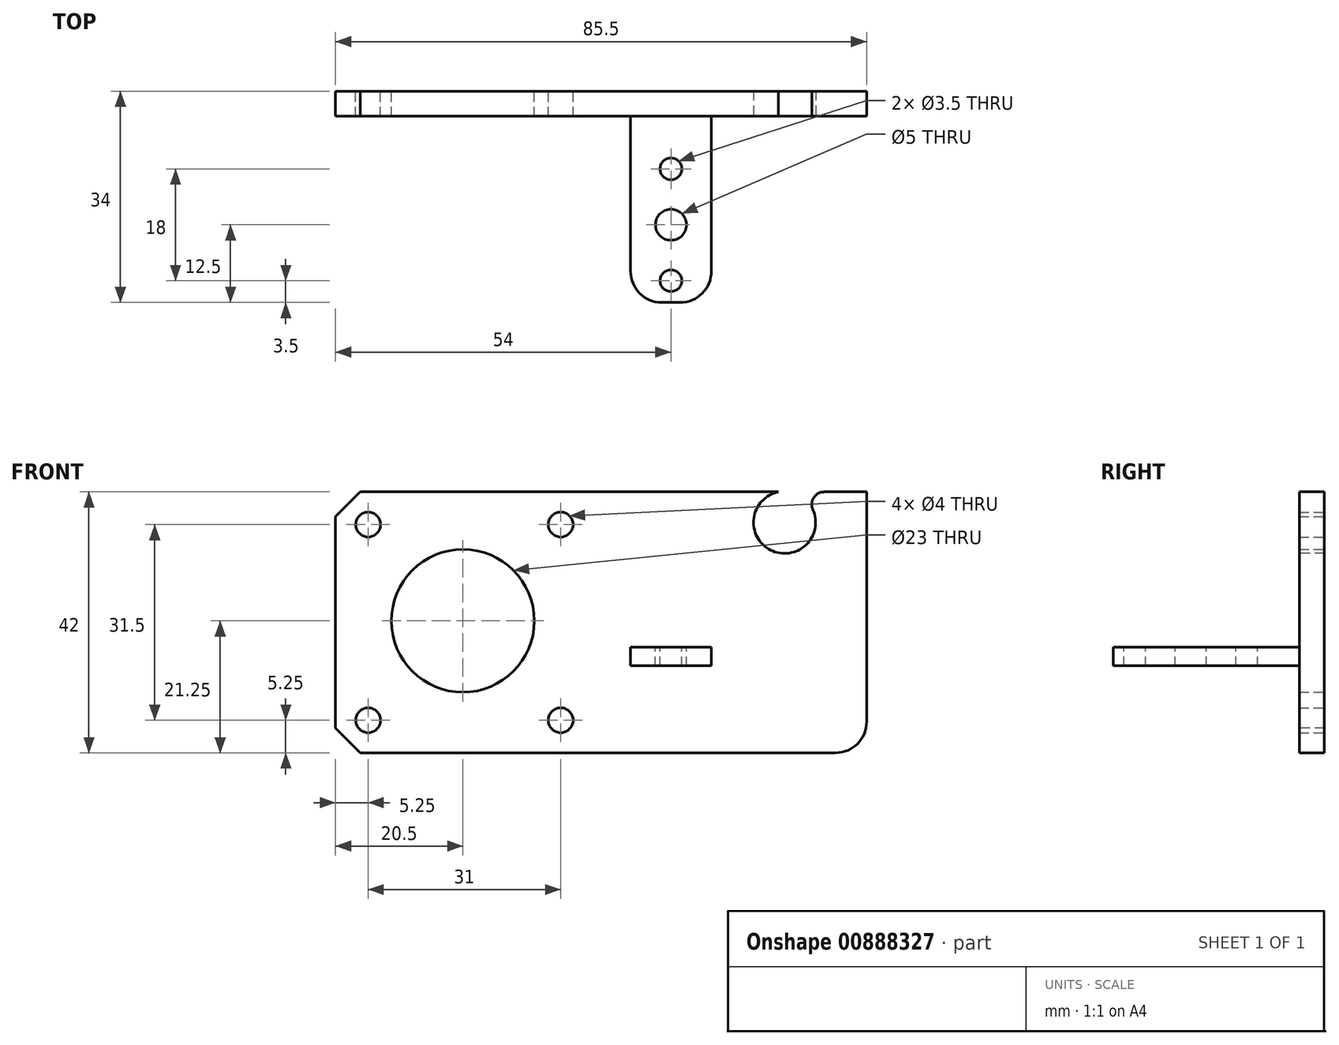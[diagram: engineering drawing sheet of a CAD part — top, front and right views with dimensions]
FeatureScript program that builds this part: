
annotation { "Feature Type Name" : "Feature", "Feature Type Description" : "" }
export const myFeature = defineFeature(function(context is Context, id is Id, definition is map)
    precondition{}
    {
        {
            var Q0;
            Q0=qCreatedBy(makeId("Front.planeOp"),FACE);
            var sketch = newSketch(context, id + "F0", { "sketchPlane" : qUnion([Q0])});
            skLineSegment(sketch, "E0.bottom", {"start": v(43, -21.25) * mm, "end": v(-20.5, -21.25) * mm});
            skLineSegment(sketch, "E0.top", {"start": v(43, 20.75) * mm, "end": v(-20.5, 20.75) * mm});
            skLineSegment(sketch, "E0.left", {"start": v(43, -21.25) * mm, "end": v(43, 20.75) * mm});
            skLineSegment(sketch, "E0.right", {"start": v(-20.5, -21.25) * mm, "end": v(-20.5, 20.75) * mm});
            skPoint(sketch, "E0.middle", {"position": v(0, 0) * mm});
            skCircle(sketch, "E1", {"center": v(0, 0) * mm, "radius": 11.5 * mm});
            skCircle(sketch, "E2", {"center": v(-15.25, 15.5) * mm, "radius": 2 * mm});
            skCircle(sketch, "E3", {"center": v(15.75, 15.5) * mm, "radius": 2 * mm});
            skCircle(sketch, "E4", {"center": v(-15.25, -16) * mm, "radius": 2 * mm});
            skCircle(sketch, "E5", {"center": v(15.75, -16) * mm, "radius": 2 * mm});
            skSolve(sketch);
        }
        {
            var Q0;
            Q0=makeQuery(id+"F0.imprint","IMPRINT",FACE,{"disambiguationData":[TD([[makeQuery(id+"F0.imprint","IMPRINT",EDGE,{"derivedFrom":sQuery(id+"F0.wireOp",EDGE,"E0.bottom")}),-1.0]])]});
            extrude(context, id + "F1", {"entities" : qUnion([Q0]), "depth" : 4 * mm, "offsetDistance" : 25 * mm});
        }
        {
            var Q0;
            Q0=makeQuery(id+"F1.opExtrude","SWEPT_EDGE",EDGE,{"disambiguationData":[OSD([sQuery(id+"F0.wireOp",EDGE,"E0.bottom"),sQuery(id+"F0.wireOp",EDGE,"E0.right")])]});
            var Q1;
            Q1=makeQuery(id+"F1.opExtrude","SWEPT_EDGE",EDGE,{"disambiguationData":[OSD([sQuery(id+"F0.wireOp",EDGE,"E0.top"),sQuery(id+"F0.wireOp",EDGE,"E0.right")])]});
            chamfer(context, id + "F2", {"entities" : qUnion([Q0, Q1]), "width" : 4 * mm, "tangentPropagation" : true});
        }
        {
            var Q0;
            Q0=makeQuery(id+"F1.opExtrude","CAP_FACE",FACE,{"disambiguationData":[OSD([sQuery(id+"F0.wireOp",EDGE,"E0.bottom"),sQuery(id+"F0.wireOp",EDGE,"E0.top"),sQuery(id+"F0.wireOp",EDGE,"E0.left"),sQuery(id+"F0.wireOp",EDGE,"E0.right"),sQuery(id+"F0.wireOp",EDGE,"E1"),sQuery(id+"F0.wireOp",EDGE,"E2"),sQuery(id+"F0.wireOp",EDGE,"E3"),sQuery(id+"F0.wireOp",EDGE,"E4"),sQuery(id+"F0.wireOp",EDGE,"E5")])],"isStart":false});
            var sketch = newSketch(context, id + "F3", { "sketchPlane" : qUnion([Q0])});
            skLineSegment(sketch, "E6.bottom", {"start": v(27, -4.25) * mm, "end": v(40, -4.25) * mm});
            skLineSegment(sketch, "E6.top", {"start": v(27, -7.25) * mm, "end": v(40, -7.25) * mm});
            skLineSegment(sketch, "E6.left", {"start": v(27, -4.25) * mm, "end": v(27, -7.25) * mm});
            skLineSegment(sketch, "E6.right", {"start": v(40, -4.25) * mm, "end": v(40, -7.25) * mm});
            skSolve(sketch);
        }
        {
            var Q0;
            Q0=qSketchRegion(id+"F3",true);
            extrude(context, id + "F4", {"entities" : qUnion([Q0]), "operationType" : NewBodyOperationType.ADD, "depth" : 30 * mm, "offsetDistance" : 25 * mm});
        }
        {
            var Q0;
            Q0=makeQuery(id+"F4.opExtrude","CAP_EDGE",EDGE,{"disambiguationData":[OSD([sQuery(id+"F3.wireOp",EDGE,"E6.right")])],"isStart":false});
            var Q1;
            Q1=makeQuery(id+"F4.opExtrude","CAP_EDGE",EDGE,{"disambiguationData":[OSD([sQuery(id+"F3.wireOp",EDGE,"E6.left")])],"isStart":false});
            fillet(context, id + "F5", {"entities" : qUnion([Q0, Q1]), "radius" : 5 * mm, "tangentPropagation" : true, "allowEdgeOverflow" : false});
        }
        {
            var Q0;
            Q0=makeQuery(id+"F4.opExtrude","SWEPT_FACE",FACE,{"disambiguationData":[OSD([sQuery(id+"F3.wireOp",EDGE,"E6.bottom")])]});
            var sketch = newSketch(context, id + "F6", { "sketchPlane" : qUnion([Q0])});
            skCircle(sketch, "E7", {"center": v(33.5, -21.5) * mm, "radius": 2.5 * mm});
            skCircle(sketch, "E8", {"center": v(33.5, -30.5) * mm, "radius": 1.75 * mm});
            skCircle(sketch, "E9", {"center": v(33.5, -12.5) * mm, "radius": 1.75 * mm});
            skLineSegment(sketch, "E10", {"start": v(33.5, -4) * mm, "end": v(33.5, -34) * mm, "construction": true});
            skSolve(sketch);
        }
        {
            var Q0;
            Q0=qSketchRegion(id+"F6",true);
            extrude(context, id + "F7", {"entities" : qUnion([Q0]), "operationType" : NewBodyOperationType.REMOVE, "endBound" : BoundingType.UP_TO_NEXT, "oppositeDirection" : true, "depth" : 25 * mm, "offsetDistance" : 25 * mm});
        }
        {
            var Q0;
            Q0=makeQuery(id+"F1.opExtrude","SWEPT_FACE",FACE,{"disambiguationData":[OSD([sQuery(id+"F0.wireOp",EDGE,"E0.left")])]});
            var sketch = newSketch(context, id + "F8", { "sketchPlane" : qUnion([Q0])});
            skLineSegment(sketch, "E11.bottom", {"start": v(-4, 20.75) * mm, "end": v(0, 20.75) * mm});
            skLineSegment(sketch, "E11.top", {"start": v(-4, -21.25) * mm, "end": v(0, -21.25) * mm});
            skLineSegment(sketch, "E11.left", {"start": v(-4, 20.75) * mm, "end": v(-4, -21.25) * mm});
            skLineSegment(sketch, "E11.right", {"start": v(0, 20.75) * mm, "end": v(0, -21.25) * mm});
            skSolve(sketch);
        }
        {
            var Q0;
            Q0 = qSketchRegion(id + "F8", true);
            extrude(context, id + "F9", {"entities" : qUnion([Q0]), "operationType" : NewBodyOperationType.ADD, "depth" : 22 * mm, "offsetDistance" : 25 * mm});
        }
        {
            var Q0;
            Q0=makeQuery(id+"F9.opExtrude","CAP_EDGE",EDGE,{"disambiguationData":[OSD([sQuery(id+"F8.wireOp",EDGE,"E11.top")])],"isStart":false});
            fillet(context, id + "F10", {"entities" : qUnion([Q0]), "radius" : 5 * mm, "tangentPropagation" : true, "allowEdgeOverflow" : false});
        }
        {
            var Q0;
            Q0=makeQuery(id+"F9.boolean.opBoolean","MERGE",FACE,{"derivedFrom":[makeQuery(id+"F1.opExtrude","CAP_FACE",FACE,{"disambiguationData":[OSD([sQuery(id+"F0.wireOp",EDGE,"E0.bottom"),sQuery(id+"F0.wireOp",EDGE,"E0.top"),sQuery(id+"F0.wireOp",EDGE,"E0.left"),sQuery(id+"F0.wireOp",EDGE,"E0.right"),sQuery(id+"F0.wireOp",EDGE,"E1"),sQuery(id+"F0.wireOp",EDGE,"E2"),sQuery(id+"F0.wireOp",EDGE,"E3"),sQuery(id+"F0.wireOp",EDGE,"E4"),sQuery(id+"F0.wireOp",EDGE,"E5")])],"isStart":false}),makeQuery(id+"F9.opExtrude","SWEPT_FACE",FACE,{"disambiguationData":[OSD([sQuery(id+"F8.wireOp",EDGE,"E11.left")])]})]});
            var sketch = newSketch(context, id + "F11", { "sketchPlane" : qUnion([Q0])});
            skCircle(sketch, "E12", {"center": v(51.8, 15.85) * mm, "radius": 5 * mm});
            skSolve(sketch);
        }
        {
            var Q0;
            Q0 = qSketchRegion(id + "F11", true);
            extrude(context, id + "F12", {"entities" : qUnion([Q0]), "operationType" : NewBodyOperationType.REMOVE, "endBound" : BoundingType.UP_TO_NEXT, "oppositeDirection" : true, "depth" : 25 * mm, "offsetDistance" : 25 * mm});
        }
        {
            var Q0;
            Q0=makeQuery(id+"F12.boolean.opBoolean","COPY",EDGE,{"derivedFrom":makeQuery(id+"F12.opExtrude","CAP_EDGE",EDGE,{"disambiguationData":[OSD([sQuery(id+"F11.wireOp",EDGE,"E12")])],"isStart":true})});
            var Q1;
            Q1=makeQuery(id+"F12.boolean.opBoolean","COPY",EDGE,{"derivedFrom":makeQuery(id+"F12.opExtrude","CAP_EDGE",EDGE,{"disambiguationData":[OSD([sQuery(id+"F11.wireOp",EDGE,"E12")]),topologyDisambiguationEdgeConnected([makeQuery(id+"F9.boolean.opBoolean","MERGE",FACE,{"derivedFrom":[makeQuery(id+"F1.opExtrude","CAP_FACE",FACE,{"disambiguationData":[OSD([sQuery(id+"F0.wireOp",EDGE,"E0.bottom"),sQuery(id+"F0.wireOp",EDGE,"E0.top"),sQuery(id+"F0.wireOp",EDGE,"E0.left"),sQuery(id+"F0.wireOp",EDGE,"E0.right"),sQuery(id+"F0.wireOp",EDGE,"E1"),sQuery(id+"F0.wireOp",EDGE,"E2"),sQuery(id+"F0.wireOp",EDGE,"E3"),sQuery(id+"F0.wireOp",EDGE,"E4"),sQuery(id+"F0.wireOp",EDGE,"E5")])],"isStart":true}),makeQuery(id+"F9.opExtrude","SWEPT_FACE",FACE,{"disambiguationData":[OSD([sQuery(id+"F8.wireOp",EDGE,"E11.right")])]})]})])],"isStart":false})});
            var Q2;
            Q2=makeQuery(id+"F12.boolean.opBoolean","COPY",EDGE,{"derivedFrom":makeQuery(id+"F12.opExtrude","CAP_EDGE",EDGE,{"disambiguationData":[OSD([sQuery(id+"F11.wireOp",EDGE,"E12")]),topologyDisambiguationEdgeConnected([makeQuery(id+"F9.boolean.opBoolean","MERGE",FACE,{"derivedFrom":[makeQuery(id+"F1.opExtrude","SWEPT_FACE",FACE,{"disambiguationData":[OSD([sQuery(id+"F0.wireOp",EDGE,"E0.top")])]}),makeQuery(id+"F9.opExtrude","SWEPT_FACE",FACE,{"disambiguationData":[OSD([sQuery(id+"F8.wireOp",EDGE,"E11.bottom")])]})]})]),OD(1.0)],"isStart":false})});
            var Q3;
            Q3=makeQuery(id+"F12.boolean.opBoolean","COPY",EDGE,{"derivedFrom":makeQuery(id+"F12.opExtrude","CAP_EDGE",EDGE,{"disambiguationData":[OSD([sQuery(id+"F11.wireOp",EDGE,"E12")]),topologyDisambiguationEdgeConnected([makeQuery(id+"F9.boolean.opBoolean","MERGE",FACE,{"derivedFrom":[makeQuery(id+"F1.opExtrude","SWEPT_FACE",FACE,{"disambiguationData":[OSD([sQuery(id+"F0.wireOp",EDGE,"E0.top")])]}),makeQuery(id+"F9.opExtrude","SWEPT_FACE",FACE,{"disambiguationData":[OSD([sQuery(id+"F8.wireOp",EDGE,"E11.bottom")])]})]})]),OD(0.0)],"isStart":false})});
            fillet(context, id + "F13", {"entities" : qUnion([Q0, Q1, Q2, Q3]), "radius" : 2 * mm, "tangentPropagation" : true, "allowEdgeOverflow" : false});
        }
    });
